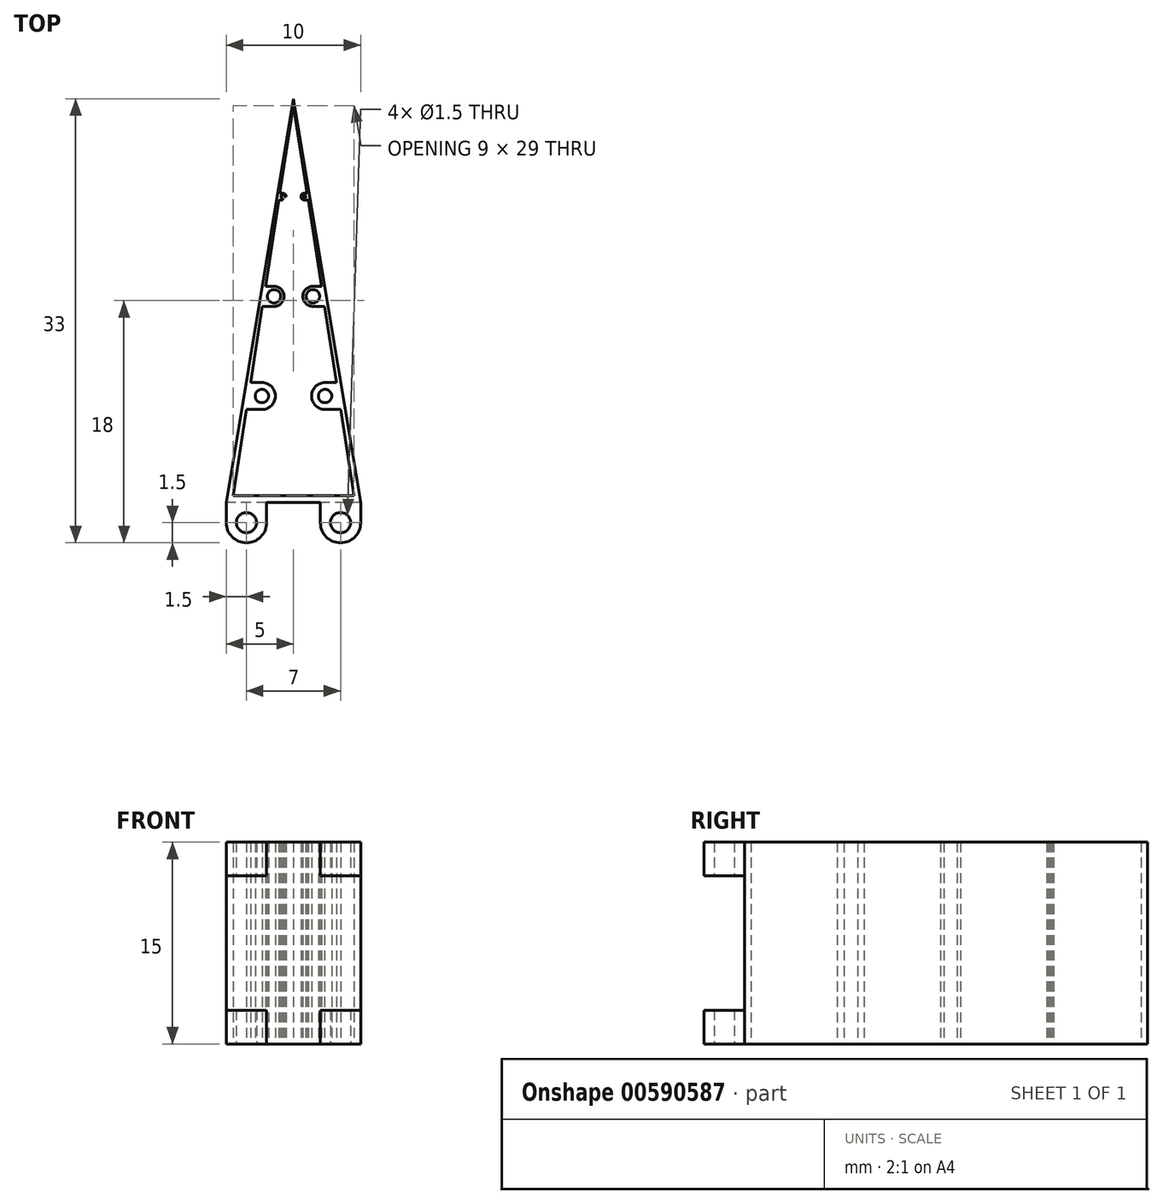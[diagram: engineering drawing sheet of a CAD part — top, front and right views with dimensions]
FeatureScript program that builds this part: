
annotation { "Feature Type Name" : "Feature", "Feature Type Description" : "" }
export const myFeature = defineFeature(function(context is Context, id is Id, definition is map)
    precondition{}
    {
        {
            var Q0;
            Q0=qCreatedBy(makeId("Top.planeOp"),FACE);
            var sketch = newSketch(context, id + "F0", { "sketchPlane" : qUnion([Q0])});
            skLineSegment(sketch, "E0", {"start": v(0, 0) * mm, "end": v(10, 0) * mm});
            skLineSegment(sketch, "E1", {"start": v(0, 0) * mm, "end": v(0, 0.5) * mm});
            skLineSegment(sketch, "E2", {"start": v(0, 0) * mm, "end": v(0.5, 0) * mm});
            skLineSegment(sketch, "E3", {"start": v(10, 0) * mm, "end": v(9.5, 0) * mm});
            skLineSegment(sketch, "E4", {"start": v(-0.1, 0) * mm, "end": v(0, 0) * mm});
            skPoint(sketch, "E4.startSnap0", {"position": v(0.25, 0) * mm});
            skLineSegment(sketch, "E5", {"start": v(10, 0) * mm, "end": v(8.5, 0) * mm});
            skArc(sketch, "E6", {"start": v(7, -1.5) * mm, "mid": v(8.5, -3) * mm, "end": v(10, -1.5) * mm});
            skLineSegment(sketch, "E7", {"start": v(10, -1.5) * mm, "end": v(10, 0) * mm});
            skLineSegment(sketch, "E8", {"start": v(7, -1.5) * mm, "end": v(7, 0) * mm});
            skCircle(sketch, "E9", {"center": v(8.5, -1.5) * mm, "radius": 0.75 * mm});
            skPoint(sketch, "E10.trimOffspring.end.orphan", {"position": v(8.5, -3) * mm});
            skPoint(sketch, "E11.trimOffspring.end.orphan", {"position": v(1.4, -3) * mm});
            skPoint(sketch, "E11.trimOffspring.start.orphan", {"position": v(1.4, -1.5) * mm});
            skLineSegment(sketch, "E12.trimOffspring", {"start": v(0.5, 0) * mm, "end": v(1.4, 0) * mm});
            skLineSegment(sketch, "E13", {"start": v(0, 0) * mm, "end": v(1.5, 0) * mm});
            skCircle(sketch, "E14", {"center": v(1.5, -1.5) * mm, "radius": 0.75 * mm});
            skArc(sketch, "E15", {"start": v(0, -1.5) * mm, "mid": v(1.5, -3) * mm, "end": v(3, -1.5) * mm});
            skLineSegment(sketch, "E16", {"start": v(1.5, -1.5) * mm, "end": v(1.4, -1.5) * mm});
            skLineSegment(sketch, "E17", {"start": v(0, -1.5) * mm, "end": v(0, 0) * mm});
            skLineSegment(sketch, "E18", {"start": v(3, -1.5) * mm, "end": v(3, 0) * mm});
            skPoint(sketch, "E19.trimOffspring.end.orphan", {"position": v(1.5, -3) * mm});
            skLineSegment(sketch, "E20", {"start": v(10, 0) * mm, "end": v(10, 2.71) * mm});
            skLineSegment(sketch, "E21", {"start": v(10, 2.71) * mm, "end": v(10, 0) * mm});
            skLineSegment(sketch, "E22", {"start": v(0, 0) * mm, "end": v(5, 30) * mm});
            skLineSegment(sketch, "E23", {"start": v(5, 30) * mm, "end": v(10, 0) * mm});
            skPoint(sketch, "E24.orphan", {"position": v(0, 30) * mm});
            skPoint(sketch, "E25.orphan", {"position": v(10, 30) * mm});
            skLineSegment(sketch, "E26", {"start": v(0.5, 0) * mm, "end": v(0.5, 0.5) * mm});
            skLineSegment(sketch, "E27", {"start": v(9.5, 0) * mm, "end": v(9.5, 0.5) * mm});
            skLineSegment(sketch, "E28", {"start": v(9.5, 0.5) * mm, "end": v(0.5, 0.5) * mm});
            skLineSegment(sketch, "E29", {"start": v(0.5, 0.5) * mm, "end": v(0.5, 3) * mm});
            skLineSegment(sketch, "E30", {"start": v(4.92, 29.5) * mm, "end": v(5.08, 29.5) * mm});
            skLineSegment(sketch, "E31", {"start": v(9.5, 3) * mm, "end": v(9.5, 0.5) * mm});
            skLineSegment(sketch, "E32", {"start": v(9.5, 0.5) * mm, "end": v(5, 29.5) * mm});
            skLineSegment(sketch, "E33", {"start": v(5, 29.5) * mm, "end": v(0.5, 0.5) * mm});
            skPoint(sketch, "E34.orphan", {"position": v(0.5, 29.5) * mm});
            skPoint(sketch, "E35.orphan", {"position": v(9.5, 29.5) * mm});
            skLineSegment(sketch, "E36", {"start": v(0.5, 0.5) * mm, "end": v(1.65, 7.91) * mm});
            skLineSegment(sketch, "E37", {"start": v(1.65, 7.91) * mm, "end": v(2.8, 15.32) * mm});
            skLineSegment(sketch, "E38", {"start": v(2.8, 15.32) * mm, "end": v(4.3, 15.32) * mm});
            skLineSegment(sketch, "E39", {"start": v(7.2, 15.32) * mm, "end": v(6.05, 22.73) * mm});
            skLineSegment(sketch, "E40", {"start": v(6.05, 22.73) * mm, "end": v(5.55, 22.73) * mm});
            skCircle(sketch, "E41", {"center": v(2.65, 7.91) * mm, "radius": 0.5 * mm});
            skArc(sketch, "E42", {"start": v(2.65, 6.91) * mm, "mid": v(3.65, 7.91) * mm, "end": v(2.65, 8.91) * mm});
            skLineSegment(sketch, "E43", {"start": v(2.65, 8.91) * mm, "end": v(1.8, 8.91) * mm});
            skLineSegment(sketch, "E44", {"start": v(2.65, 7.91) * mm, "end": v(2.65, 7.41) * mm});
            skLineSegment(sketch, "E45", {"start": v(2.65, 6.91) * mm, "end": v(1.5, 6.91) * mm});
            skPoint(sketch, "E46.trimOffspring.end.orphan", {"position": v(3.65, 7.91) * mm});
            skArc(sketch, "E47", {"start": v(7.35, 8.91) * mm, "mid": v(6.35, 7.91) * mm, "end": v(7.35, 6.91) * mm});
            skCircle(sketch, "E48", {"center": v(7.35, 7.91) * mm, "radius": 0.5 * mm});
            skLineSegment(sketch, "E49", {"start": v(7.35, 8.91) * mm, "end": v(8.2, 8.91) * mm});
            skLineSegment(sketch, "E50", {"start": v(7.35, 6.91) * mm, "end": v(8.5, 6.91) * mm});
            skPoint(sketch, "E51.start.orphan", {"position": v(8.35, 7.91) * mm});
            skPoint(sketch, "E52.trimOffspring.end.orphan", {"position": v(6.35, 7.91) * mm});
            skLineSegment(sketch, "E53", {"start": v(7.2, 15.32) * mm, "end": v(5.7, 15.32) * mm});
            skArc(sketch, "E54", {"start": v(3.55, 14.57) * mm, "mid": v(4.3, 15.32) * mm, "end": v(3.55, 16.07) * mm});
            skCircle(sketch, "E55", {"center": v(3.55, 15.32) * mm, "radius": 0.5 * mm});
            skArc(sketch, "E56", {"start": v(6.45, 16.07) * mm, "mid": v(5.7, 15.32) * mm, "end": v(6.45, 14.57) * mm});
            skCircle(sketch, "E57", {"center": v(6.45, 15.32) * mm, "radius": 0.5 * mm});
            skLineSegment(sketch, "E58", {"start": v(3.55, 15.32) * mm, "end": v(3.55, 16.07) * mm});
            skLineSegment(sketch, "E59", {"start": v(3.55, 16.07) * mm, "end": v(2.92, 16.07) * mm});
            skLineSegment(sketch, "E60", {"start": v(6.45, 16.07) * mm, "end": v(7.08, 16.07) * mm});
            skLineSegment(sketch, "E61", {"start": v(3.55, 15.32) * mm, "end": v(3.55, 14.57) * mm});
            skLineSegment(sketch, "E62", {"start": v(3.55, 14.57) * mm, "end": v(2.68, 14.57) * mm});
            skLineSegment(sketch, "E63", {"start": v(6.45, 14.57) * mm, "end": v(7.32, 14.57) * mm});
            skLineSegment(sketch, "E64.trimOffspring", {"start": v(5.7, 15.32) * mm, "end": v(7.2, 15.32) * mm});
            skLineSegment(sketch, "E65", {"start": v(3.95, 22.73) * mm, "end": v(4.45, 22.73) * mm});
            skArc(sketch, "E66", {"start": v(4.2, 22.48) * mm, "mid": v(4.45, 22.73) * mm, "end": v(4.2, 22.98) * mm});
            skArc(sketch, "E67", {"start": v(5.8, 22.98) * mm, "mid": v(5.55, 22.73) * mm, "end": v(5.8, 22.48) * mm});
            skCircle(sketch, "E68", {"center": v(4.2, 22.73) * mm, "radius": 0.12 * mm});
            skCircle(sketch, "E69", {"center": v(5.8, 22.73) * mm, "radius": 0.12 * mm});
            skLineSegment(sketch, "E70", {"start": v(4.2, 22.73) * mm, "end": v(4.2, 22.98) * mm});
            skLineSegment(sketch, "E71", {"start": v(4.2, 22.98) * mm, "end": v(3.99, 22.98) * mm});
            skLineSegment(sketch, "E72", {"start": v(4.2, 22.73) * mm, "end": v(4.2, 22.48) * mm});
            skLineSegment(sketch, "E73", {"start": v(4.2, 22.48) * mm, "end": v(3.91, 22.48) * mm});
            skLineSegment(sketch, "E74", {"start": v(5.8, 22.98) * mm, "end": v(6.01, 22.98) * mm});
            skLineSegment(sketch, "E75", {"start": v(5.8, 22.48) * mm, "end": v(6.09, 22.48) * mm});
            skLineSegment(sketch, "E76.trimOffspring", {"start": v(4.45, 22.73) * mm, "end": v(3.95, 22.73) * mm});
            skSolve(sketch);
        }
        {
            var Q0;
            Q0=qCreatedBy(makeId("Right.planeOp"),FACE);
            var sketch = newSketch(context, id + "F1", { "sketchPlane" : qUnion([Q0])});
            skLineSegment(sketch, "E77", {"start": v(0, 0) * mm, "end": v(0, 7.5) * mm});
            skLineSegment(sketch, "E78", {"start": v(0, 7.5) * mm, "end": v(0, 12.5) * mm});
            skLineSegment(sketch, "E79", {"start": v(0, 7.5) * mm, "end": v(0, 2.5) * mm});
            skLineSegment(sketch, "E80", {"start": v(0, 2.5) * mm, "end": v(-3, 2.5) * mm});
            skLineSegment(sketch, "E81", {"start": v(-3, 2.5) * mm, "end": v(-3, 12.5) * mm});
            skLineSegment(sketch, "E82", {"start": v(-3, 12.5) * mm, "end": v(0, 12.5) * mm});
            skSolve(sketch);
        }
        {
            var Q0;
            Q0 = qSketchRegion(id + "F0", true);
            var Q1;
            Q1=makeQuery(id+"F0.imprint","IMPRINT",FACE,{"disambiguationData":[TD([[makeQuery(id+"F0.imprint","IMPRINT",EDGE,{"derivedFrom":sQuery(id+"F0.wireOp",EDGE,"E41")}),-1.0]])]});
            var Q2;
            Q2=makeQuery(id+"F0.imprint","IMPRINT",FACE,{"disambiguationData":[TD([[makeQuery(id+"F0.imprint","IMPRINT",EDGE,{"derivedFrom":sQuery(id+"F0.wireOp",EDGE,"E47")}),1.0]])]});
            var Q3;
            {var subQ0=sQuery(id+"F0.wireOp",EDGE,"E62");Q3=makeQuery(id+"F0.imprint","IMPRINT",FACE,{"disambiguationData":[TD([[makeQuery(id+"F0.imprint","IMPRINT",EDGE,{"derivedFrom":subQ0}),-1.0]])]});}
            var Q4;
            {var subQ0=sQuery(id+"F0.wireOp",EDGE,"E54");var subQ1=sQuery(id+"F0.wireOp",EDGE,"E38");var subQ2=makeQuery(id+"F0.imprint","INTERSECT",VERTEX,{"derivedFrom":[subQ1,subQ0]});Q4=makeQuery(id+"F0.imprint","IMPRINT",FACE,{"disambiguationData":[TD([[makeQuery(id+"F0.imprint","IMPRINT",EDGE,{"disambiguationData":[TD([[subQ2,1.0]])],"derivedFrom":subQ1}),-1.0]])]});}
            var Q5;
            {var subQ0=sQuery(id+"F0.wireOp",EDGE,"E54");var subQ1=sQuery(id+"F0.wireOp",EDGE,"E38");var subQ2=makeQuery(id+"F0.imprint","INTERSECT",VERTEX,{"derivedFrom":[subQ1,subQ0]});Q5=makeQuery(id+"F0.imprint","IMPRINT",FACE,{"disambiguationData":[TD([[makeQuery(id+"F0.imprint","IMPRINT",EDGE,{"disambiguationData":[TD([[subQ2,1.0]])],"derivedFrom":subQ1}),1.0]])]});}
            var Q6;
            {var subQ5=sQuery(id+"F0.wireOp",EDGE,"E59");Q6=makeQuery(id+"F0.imprint","IMPRINT",FACE,{"disambiguationData":[TD([[makeQuery(id+"F0.imprint","IMPRINT",EDGE,{"derivedFrom":subQ5}),1.0]])]});}
            var Q7;
            {var subQ0=sQuery(id+"F0.wireOp",EDGE,"E60");Q7=makeQuery(id+"F0.imprint","IMPRINT",FACE,{"disambiguationData":[TD([[makeQuery(id+"F0.imprint","IMPRINT",EDGE,{"derivedFrom":subQ0}),-1.0]])]});}
            var Q8;
            {var subQ6=sQuery(id+"F0.wireOp",EDGE,"E63");Q8=makeQuery(id+"F0.imprint","IMPRINT",FACE,{"disambiguationData":[TD([[makeQuery(id+"F0.imprint","IMPRINT",EDGE,{"derivedFrom":subQ6}),1.0]])]});}
            var Q9;
            {var subQ0=sQuery(id+"F0.wireOp",EDGE,"E73");Q9=makeQuery(id+"F0.imprint","IMPRINT",FACE,{"disambiguationData":[TD([[makeQuery(id+"F0.imprint","IMPRINT",EDGE,{"derivedFrom":subQ0}),-1.0]])]});}
            var Q10;
            {var subQ3=sQuery(id+"F0.wireOp",EDGE,"E76.trimOffspring");var subQ5=sQuery(id+"F0.wireOp",EDGE,"E68");var subQ6=makeQuery(id+"F0.imprint","INTERSECT",VERTEX,{"disambiguationData":[OD(0.0)],"derivedFrom":[subQ5,subQ3]});Q10=makeQuery(id+"F0.imprint","IMPRINT",FACE,{"disambiguationData":[TD([[makeQuery(id+"F0.imprint","IMPRINT",EDGE,{"disambiguationData":[TD([[subQ6,1.0]])],"derivedFrom":subQ5}),-1.0]])]});}
            var Q11;
            {var subQ0=sQuery(id+"F0.wireOp",EDGE,"E70");var subQ5=sQuery(id+"F0.wireOp",EDGE,"E68");var subQ6=makeQuery(id+"F0.imprint","INTERSECT",VERTEX,{"derivedFrom":[subQ5,subQ0]});Q11=makeQuery(id+"F0.imprint","IMPRINT",FACE,{"disambiguationData":[TD([[makeQuery(id+"F0.imprint","IMPRINT",EDGE,{"disambiguationData":[TD([[subQ6,1.0]])],"derivedFrom":subQ5}),-1.0]])]});}
            var Q12;
            {var subQ0=sQuery(id+"F0.wireOp",EDGE,"E71");Q12=makeQuery(id+"F0.imprint","IMPRINT",FACE,{"disambiguationData":[TD([[makeQuery(id+"F0.imprint","IMPRINT",EDGE,{"derivedFrom":subQ0}),1.0]])]});}
            var Q13;
            {var subQ3=sQuery(id+"F0.wireOp",EDGE,"E74");Q13=makeQuery(id+"F0.imprint","IMPRINT",FACE,{"disambiguationData":[TD([[makeQuery(id+"F0.imprint","IMPRINT",EDGE,{"derivedFrom":subQ3}),-1.0]])]});}
            var Q14;
            {var subQ8=sQuery(id+"F0.wireOp",EDGE,"E75");Q14=makeQuery(id+"F0.imprint","IMPRINT",FACE,{"disambiguationData":[TD([[makeQuery(id+"F0.imprint","IMPRINT",EDGE,{"derivedFrom":subQ8}),1.0]])]});}
            extrude(context, id + "F2", {"entities" : qUnion([Q0, Q1, Q2, Q3, Q4, Q5, Q6, Q7, Q8, Q9, Q10, Q11, Q12, Q13, Q14]), "depth" : 15 * mm, "offsetDistance" : 25 * mm});
        }
        {
            var Q0;
            Q0=makeQuery(id+"F1.imprint","IMPRINT",FACE,{"disambiguationData":[TD([[makeQuery(id+"F1.imprint","IMPRINT",EDGE,{"derivedFrom":sQuery(id+"F1.wireOp",EDGE,"E78")}),1.0]])]});
            extrude(context, id + "F3", {"entities" : qUnion([Q0]), "operationType" : NewBodyOperationType.REMOVE, "depth" : 10 * mm, "offsetDistance" : 25 * mm});
        }
    });
